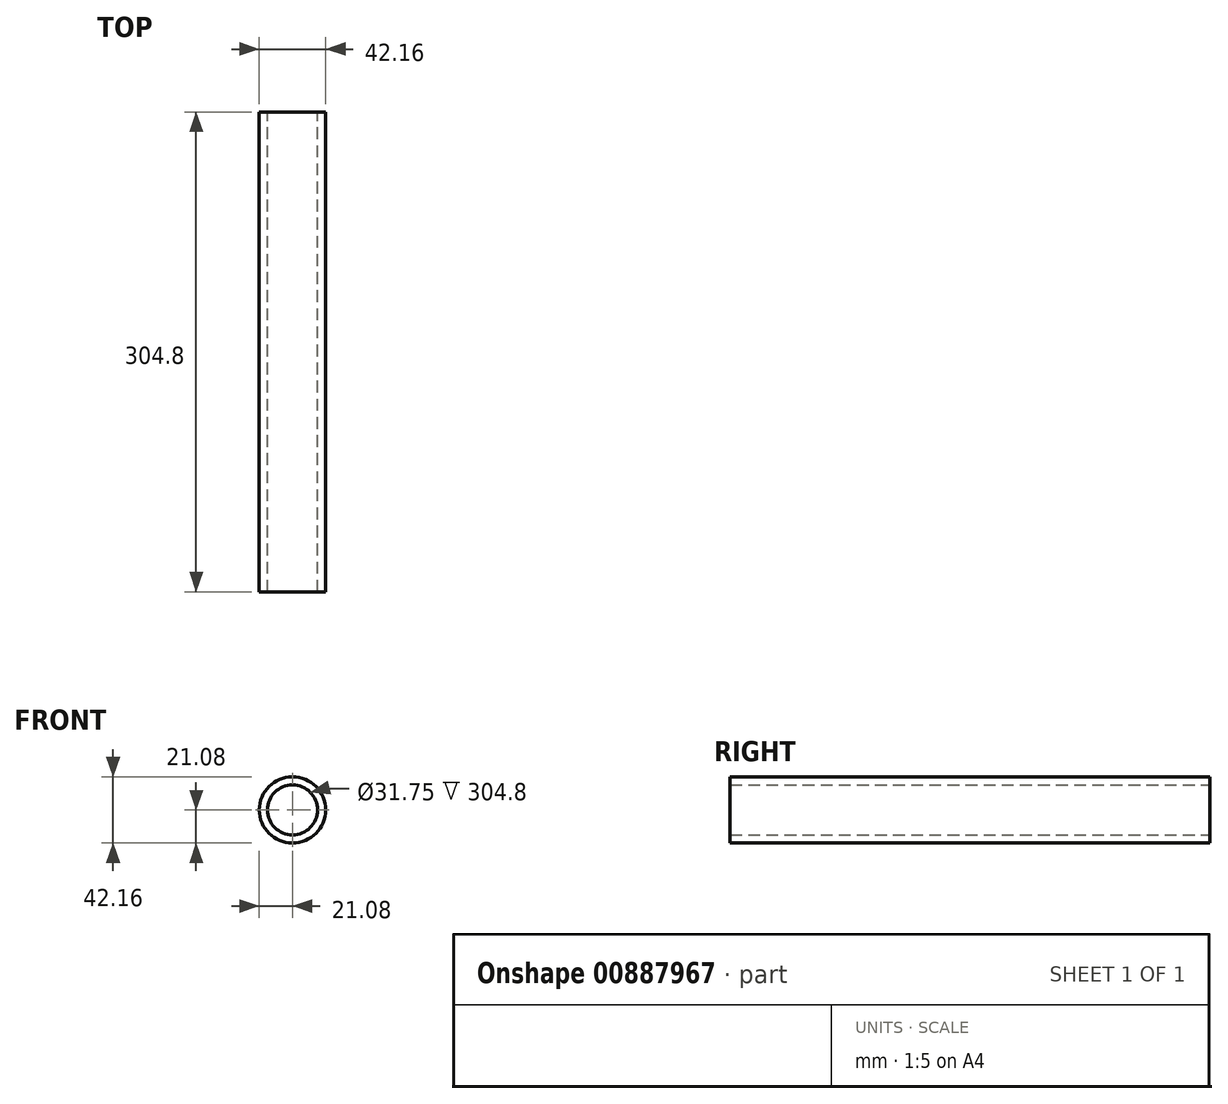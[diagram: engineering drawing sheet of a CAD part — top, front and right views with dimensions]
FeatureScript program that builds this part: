
annotation { "Feature Type Name" : "Feature", "Feature Type Description" : "" }
export const myFeature = defineFeature(function(context is Context, id is Id, definition is map)
    precondition{}
    {
        {
            var Q0;
            Q0=qCreatedBy(makeId("Front.planeOp"),FACE);
            var sketch = newSketch(context, id + "F0", { "sketchPlane" : qUnion([Q0])});
            skCircle(sketch, "E0", {"center": v(0, 0) * mm, "radius": 15.88 * mm});
            skCircle(sketch, "E1", {"center": v(0, 0) * mm, "radius": 21.08 * mm});
            skSolve(sketch);
        }
        {
            var Q0;
            Q0=makeQuery(id+"F0.imprint","IMPRINT",FACE,{"disambiguationData":[TD([[makeQuery(id+"F0.imprint","IMPRINT",EDGE,{"derivedFrom":sQuery(id+"F0.wireOp",EDGE,"E0")}),-1.0]])]});
            extrude(context, id + "F1", {"entities" : qUnion([Q0]), "depth" : 304.8 * mm, "offsetDistance" : 25.4 * mm});
        }
    });
